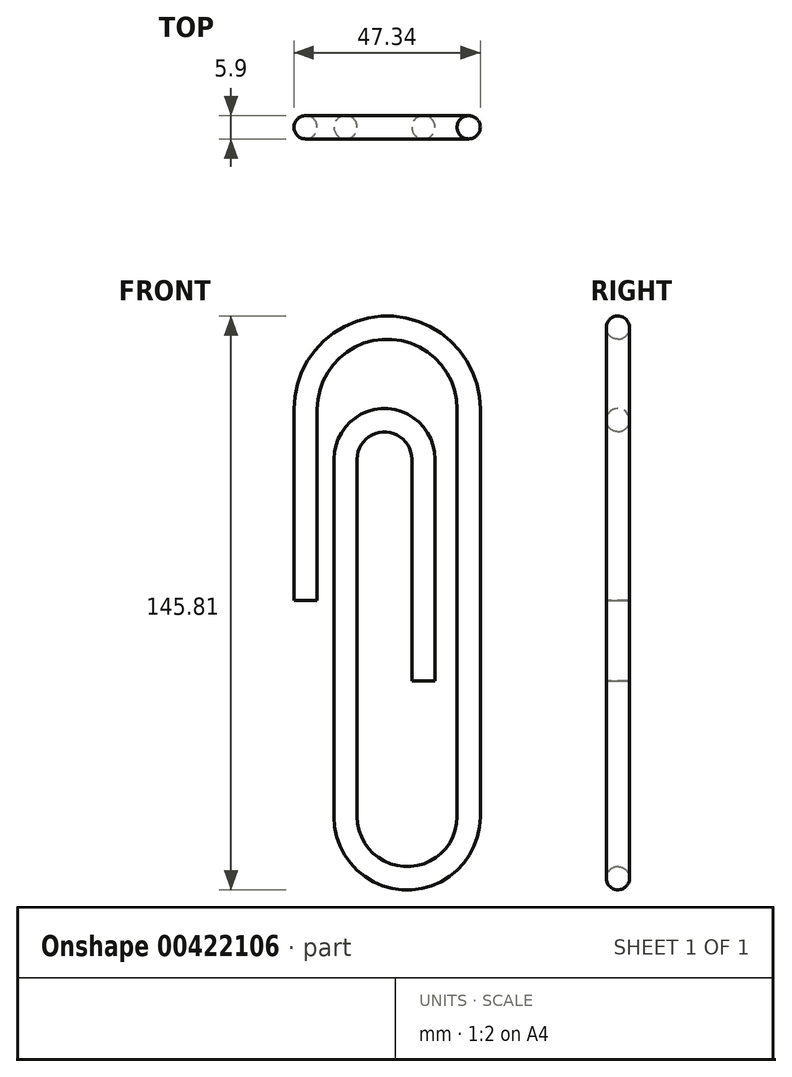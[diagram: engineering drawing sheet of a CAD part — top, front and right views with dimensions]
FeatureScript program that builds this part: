
annotation { "Feature Type Name" : "Feature", "Feature Type Description" : "" }
export const myFeature = defineFeature(function(context is Context, id is Id, definition is map)
    precondition{}
    {
        {
            var Q0;
            Q0=qCreatedBy(makeId("Top.planeOp"),FACE);
            var sketch = newSketch(context, id + "F0", { "sketchPlane" : qUnion([Q0])});
            skCircle(sketch, "E0", {"center": v(0, 0) * mm, "radius": 2.95 * mm});
            skSolve(sketch);
        }
        {
            var Q0;
            Q0=qCreatedBy(makeId("Front.planeOp"),FACE);
            var sketch = newSketch(context, id + "F1", { "sketchPlane" : qUnion([Q0])});
            skLineSegment(sketch, "E1", {"start": v(0, 0) * mm, "end": v(0, 48.66) * mm});
            skArc(sketch, "E2", {"start": v(41.43, 48.66) * mm, "mid": v(20.72, 69.37) * mm, "end": v(0, 48.66) * mm});
            skLineSegment(sketch, "E3", {"start": v(41.43, 48.66) * mm, "end": v(41.43, -54.9) * mm});
            skArc(sketch, "E4", {"start": v(10.16, -54.9) * mm, "mid": v(25.8, -70.54) * mm, "end": v(41.43, -54.9) * mm});
            skLineSegment(sketch, "E5", {"start": v(10.16, -54.9) * mm, "end": v(10.16, 35.97) * mm});
            skArc(sketch, "E6", {"start": v(29.93, 35.97) * mm, "mid": v(20.04, 45.85) * mm, "end": v(10.16, 35.97) * mm});
            skLineSegment(sketch, "E7", {"start": v(29.93, 35.97) * mm, "end": v(29.93, -20.38) * mm});
            skSolve(sketch);
        }
        {
            var Q0;
            Q0=makeQuery(id+"F0.imprint","IMPRINT",FACE,{"disambiguationData":[TD([[makeQuery(id+"F0.imprint","IMPRINT",EDGE,{"derivedFrom":sQuery(id+"F0.wireOp",EDGE,"E0")}),1.0]])]});
            var Q1;
            Q1=sQuery(id+"F1.wireOp",EDGE,"E1");
            var Q2;
            Q2=sQuery(id+"F1.wireOp",EDGE,"E2");
            var Q3;
            Q3=sQuery(id+"F1.wireOp",EDGE,"E3");
            var Q4;
            Q4=sQuery(id+"F1.wireOp",EDGE,"E4");
            var Q5;
            Q5=sQuery(id+"F1.wireOp",EDGE,"E5");
            var Q6;
            Q6=sQuery(id+"F1.wireOp",EDGE,"E6");
            var Q7;
            Q7=sQuery(id+"F1.wireOp",EDGE,"E7");
            sweep(context, id + "F2", {"profiles" : qUnion([Q0]), "path" : qUnion([Q1, Q2, Q3, Q4, Q5, Q6, Q7])});
        }
    });
